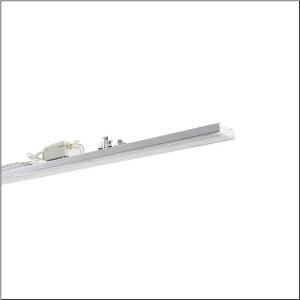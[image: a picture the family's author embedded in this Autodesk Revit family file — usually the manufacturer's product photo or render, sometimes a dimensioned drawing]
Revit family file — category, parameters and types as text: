
# Revit family: licross_21_recessed_mo_52tl14de445g
name_source: partatom
category: Lighting Fixtures
units: mm (PartAtom-declared; Revit-internal decimal feet)

## family parameters
Cut with Voids When Loaded = No
Host = Face
Light Source = No
Part Type = Normal
Room Calculation Point = No
Round Connector Dimension = Use Diameter
Shared = No

## types (1)
- --- (1 x LED, 4730 lm, 29.9 W, 4000K)
    Apparent Load = 30 VA
    CIE Flux Codes = 56 84 97 100 100
    Color Rendering = 80
    Color Temperature = 4000K
    Default Elevation = 1800 mm
    Description = Licross 21 Recessed MO, luminaire insert, of sheet steel, galvanised, coil coated, white, length: 750mm, width: 66mm, height: 67mm, LED rated luminous flux: 4.730lm, light colour: 840, SDCM (Standard Deviation of Colour Matching)MacAdam ≤ 3 SDCM (initial), control gear: DALI 2, with plug, 5-pole, with phase selection, mains connection: 220..240V, AC, 50/60Hz, rated input power: 30W, internal wiring halogen-free, primary light control with lens, of plastic, primary optical cover: cover, of PMMA, light emission: direct distribution, primary light characteristic: asymmetric, protection rating (complete): IP40, insulation class (complete): insulation class I (protective earthing), certification: CE, ENEC, VDE, UKCA, protection symbol: D if used in an environment without relevant dust loads with corresponding accessories, impact resistance: IK06, permissible ambient temperature for indoor applications: -25..+35°C, corresponds to IFS (International Featured Standards) requirements for safety and quality in the food industry, reducing of maximum allowable ambient temperature of 5°C with ceiling mounting, LABS conformity tested according to VDMA 24364:2018-05, The light source and the operating device comply with the requirements of the Ecodesign Regulation (EU) 2019/2020 and are replaceable in accordance with this regulation, packaging unit: 1 piece
    Height = 58 mm
    Lamp = 1 x LED
    Lamp Light Flux = 4730 lm
    Lamp Power = 29.9 W
    Lamp count = 1
    Length = 750 mm
    Luminous efficacy = 158 lm/W
    Manufacturer = Siteco
    ModVariant = No
    Model = 52TL14DE445G
    Mounting Place = Ceiling
    Mounting Type = Pendant
    Number of Poles = 1
    OnlyDefault = Yes
    Power Factor = 1
    Product Name = Licross 21 Recessed MO
    Product group = luminaire insert | ceiling pendant
    ProductGroupID = 901
    Protection Class = Protection class I
    Protection Degree = IP 40
    RLX_Detail_Level = 1
    RLX_Emergency_Light_Flux = 0 lm
    RLX_Emergency_Type = 0
    RLX_Emergency_Type_DB = No
    RlxData = <blob elided: 29325 chars, md5=3e56a63b>
    Socket = socket
    Standby Power = 0 W
    System Light Flux = 4730 lm
    System Power = 30 W
    Type Comments = factory setting: luminous flux: 100 % | dim-lin: 254 | 390 mA
    Type Image = l_1296930.jpg
    URL = http://relux.com
    VarID = @adj_129607
    Voltage = 0 V
    Weight = 0.00 kg
    Width = 66 mm

## geometry (parser evidence)
native form markers: Blend x4, Sweep x10
no freeform markers — native parametric forms only
